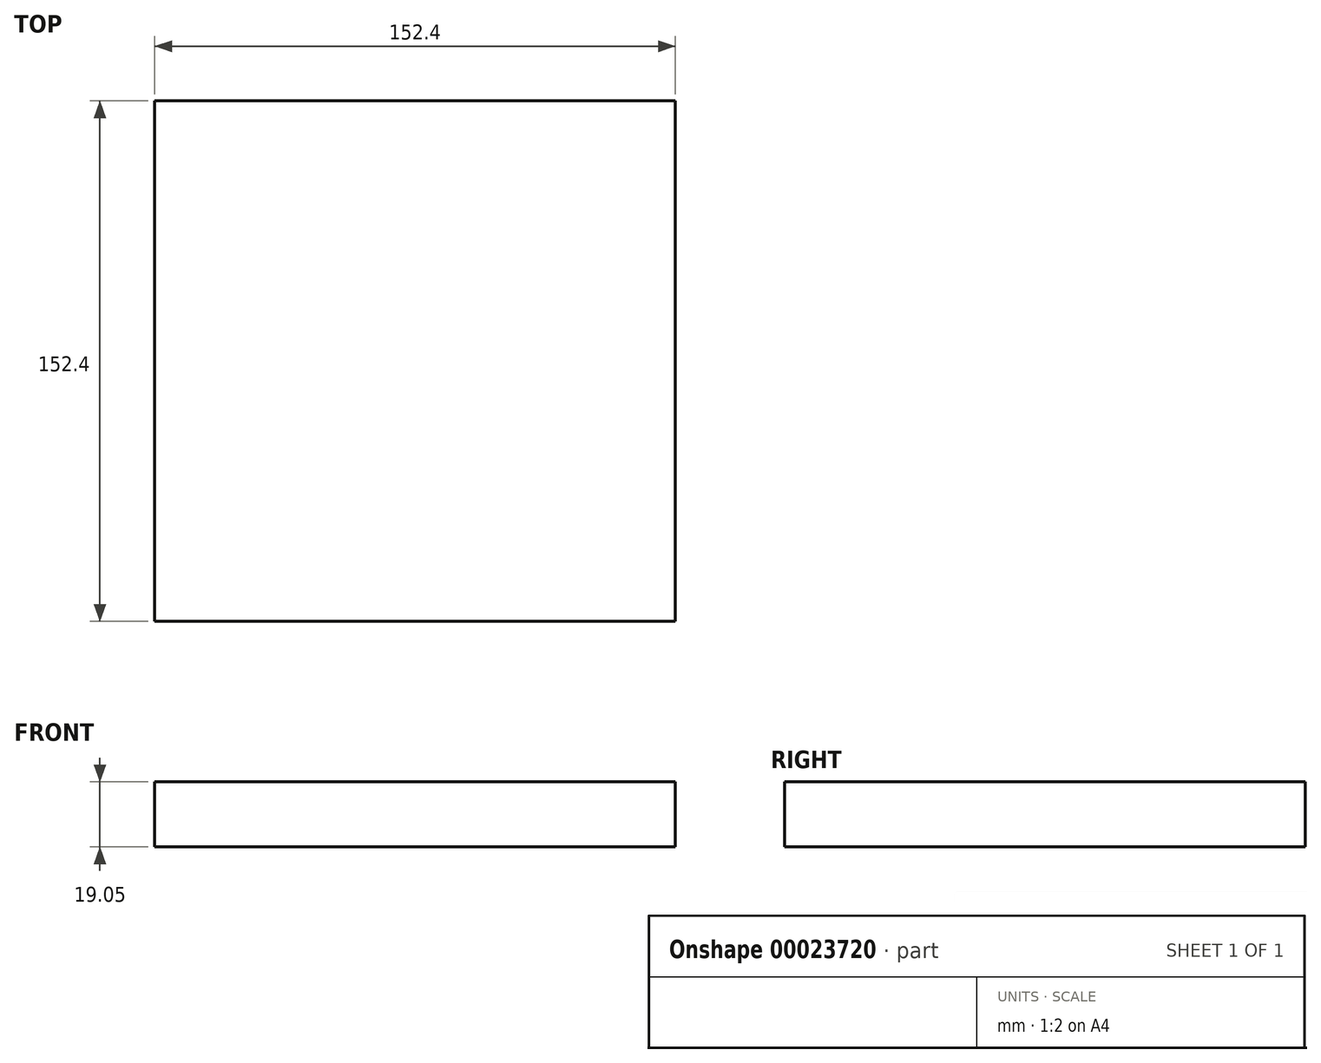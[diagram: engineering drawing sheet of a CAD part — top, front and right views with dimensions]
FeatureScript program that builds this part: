
annotation { "Feature Type Name" : "Feature", "Feature Type Description" : "" }
export const myFeature = defineFeature(function(context is Context, id is Id, definition is map)
    precondition{}
    {
        {
            var Q0;
            Q0=qCreatedBy(makeId("Top.planeOp"),FACE);
            var sketch = newSketch(context, id + "F0", { "sketchPlane" : qUnion([Q0])});
            skLineSegment(sketch, "E0.rect.bottom", {"start": v(76.2, 76.2) * mm, "end": v(-76.2, 76.2) * mm});
            skLineSegment(sketch, "E0.rect.top", {"start": v(76.2, -76.2) * mm, "end": v(-76.2, -76.2) * mm});
            skLineSegment(sketch, "E0.rect.left", {"start": v(76.2, 76.2) * mm, "end": v(76.2, -76.2) * mm});
            skLineSegment(sketch, "E0.rect.right", {"start": v(-76.2, 76.2) * mm, "end": v(-76.2, -76.2) * mm});
            skPoint(sketch, "E0.rect.middle", {"position": v(0, 0) * mm});
            skSolve(sketch);
        }
        {
            var Q0;
            Q0 = qSketchRegion(id + "F0", true);
            extrude(context, id + "F1", {"entities" : qUnion([Q0]), "depth" : 19.05 * mm});
        }
    });
